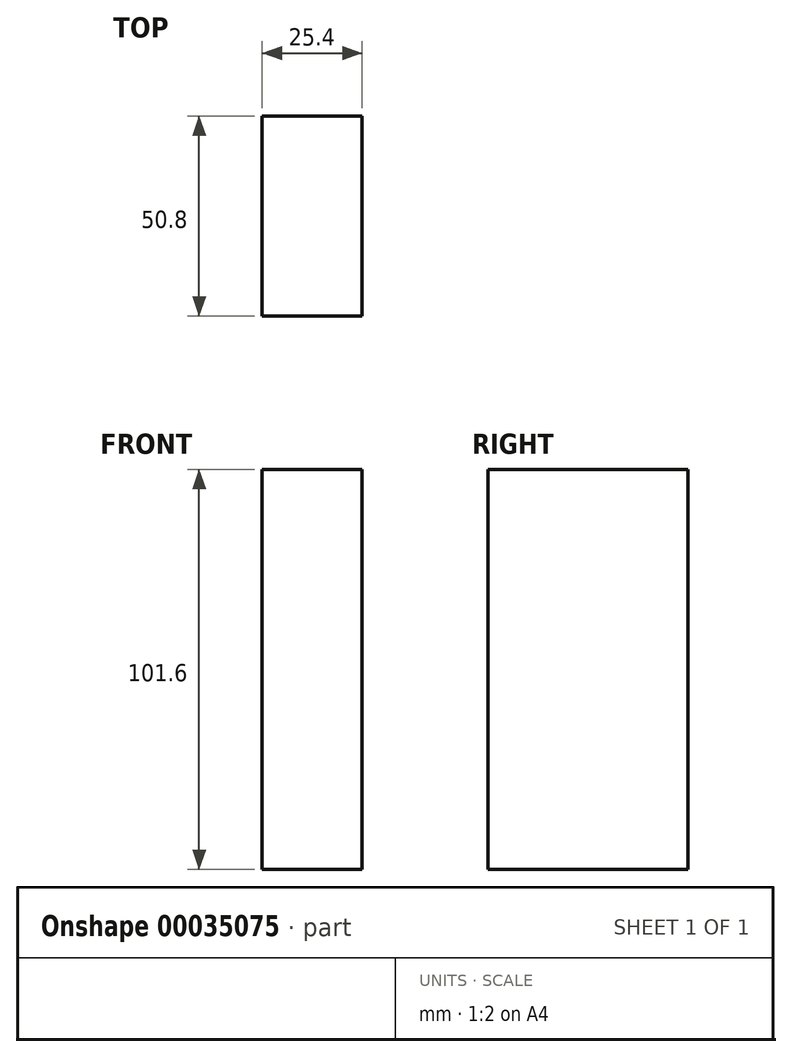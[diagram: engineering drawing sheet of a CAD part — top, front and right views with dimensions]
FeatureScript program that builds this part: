
annotation { "Feature Type Name" : "Feature", "Feature Type Description" : "" }
export const myFeature = defineFeature(function(context is Context, id is Id, definition is map)
    precondition{}
    {
        {
            var Q0;
            Q0=qCreatedBy(makeId("Right.planeOp"),FACE);
            var sketch = newSketch(context, id + "F0", { "sketchPlane" : qUnion([Q0])});
            skLineSegment(sketch, "E0.bottom", {"start": v(-17.63, 83.18) * mm, "end": v(33.17, 83.18) * mm});
            skLineSegment(sketch, "E0.top", {"start": v(-17.63, -18.42) * mm, "end": v(33.17, -18.42) * mm});
            skLineSegment(sketch, "E0.left", {"start": v(-17.63, 83.18) * mm, "end": v(-17.63, -18.42) * mm});
            skLineSegment(sketch, "E0.right", {"start": v(33.17, 83.18) * mm, "end": v(33.17, -18.42) * mm});
            skSolve(sketch);
        }
        {
            var Q0;
            Q0 = qSketchRegion(id + "F0", true);
            extrude(context, id + "F1", {"entities" : qUnion([Q0]), "depth" : 25.4 * mm});
        }
    });
